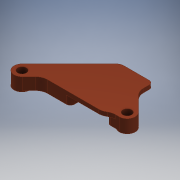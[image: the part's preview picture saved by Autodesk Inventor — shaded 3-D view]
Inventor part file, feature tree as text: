
AUTODESK INVENTOR PART (.ipt)
format: ipt  version: 2018 (Build 220112000, 112)  size: 162,816 bytes
history: native  units: mm
features: extrude x3, sketch x1, fillet x1
ambient origin geometry x8: Origin, YZ Plane, XZ Plane, XY Plane, X Axis, Y Axis, Z Axis, Center Point
bodies: Solid1 (feature_tree)
feature tree (5):
  sketch  "Sketch1"  dims[d0=7.3mm d1=3.4mm d2=15.1mm d3=7.5mm d4=2.2mm d6=8.2mm d7=4.0mm d8=4.0mm d9=45.0deg d10=3.0mm d11=0.0mm d12=0.3mm d13=0.0mm d14=2.0mm d15=0.0mm d16=3.0mm d17=1.0mm d18=2.0mm]
  extrude  "Extrusion1"  Depth=2.0mm
  extrude  "Extrusion2"  Depth=2.0mm
  extrude  "Extrusion3"  Depth=2.0mm
  fillet  "Fillet1"  Radius=2.2mm
